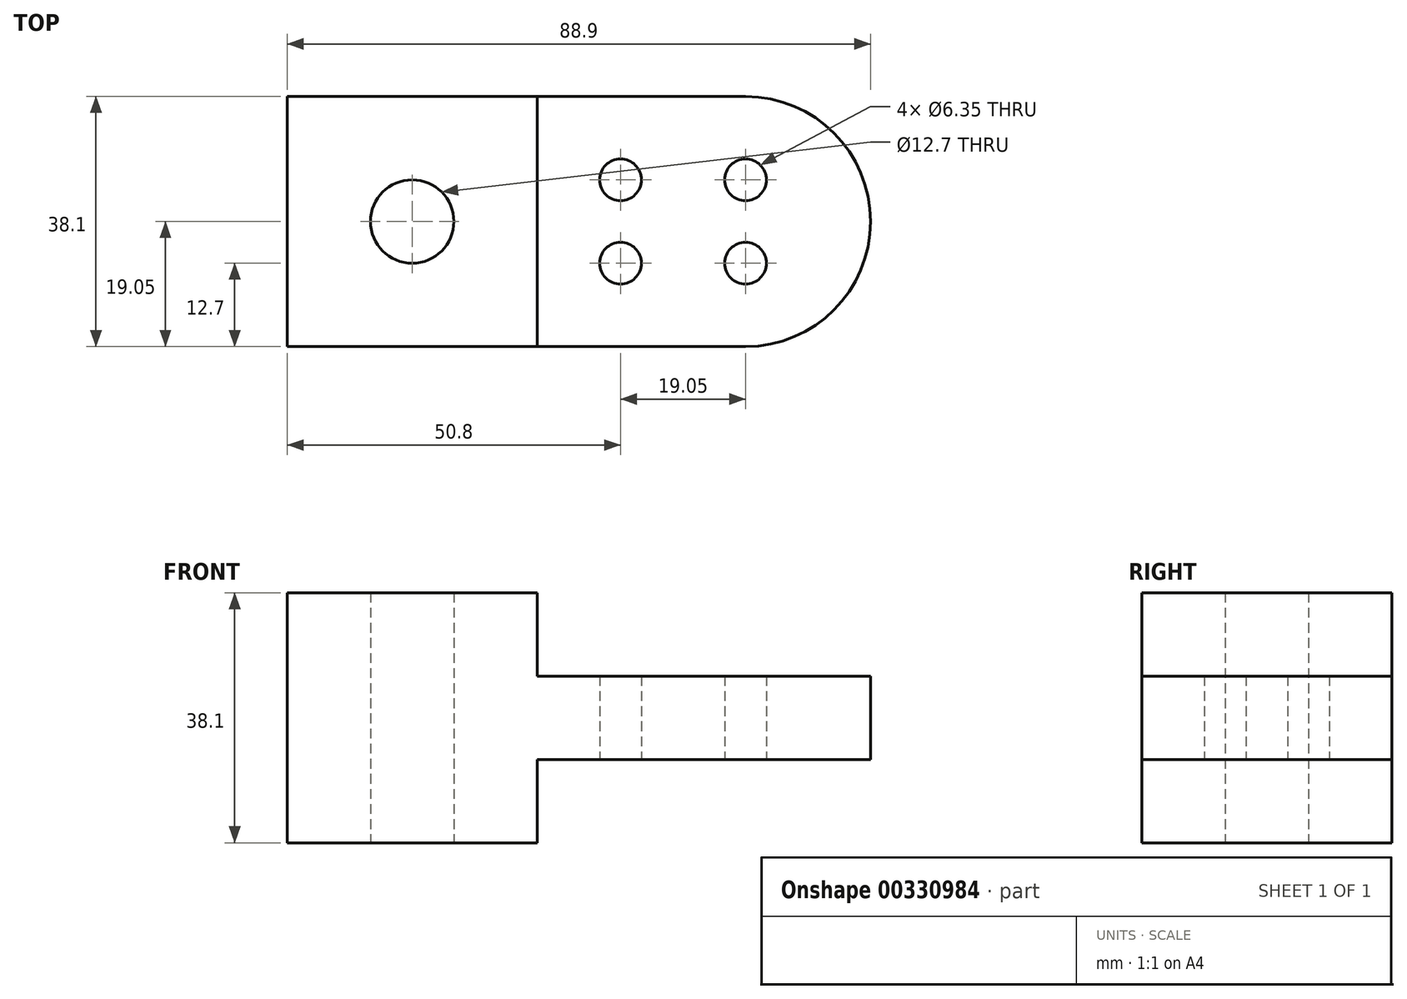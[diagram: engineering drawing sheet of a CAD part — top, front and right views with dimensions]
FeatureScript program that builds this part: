
annotation { "Feature Type Name" : "Feature", "Feature Type Description" : "" }
export const myFeature = defineFeature(function(context is Context, id is Id, definition is map)
    precondition{}
    {
        {
            var Q0;
            Q0=qCreatedBy(makeId("Top.planeOp"),FACE);
            var sketch = newSketch(context, id + "F0", { "sketchPlane" : qUnion([Q0])});
            skLineSegment(sketch, "E0.bottom", {"start": v(-19.05, 19.05) * mm, "end": v(19.05, 19.05) * mm});
            skLineSegment(sketch, "E0.top", {"start": v(-19.05, -19.05) * mm, "end": v(19.05, -19.05) * mm});
            skLineSegment(sketch, "E0.left", {"start": v(-19.05, 19.05) * mm, "end": v(-19.05, -19.05) * mm});
            skLineSegment(sketch, "E0.right", {"start": v(19.05, 19.05) * mm, "end": v(19.05, -19.05) * mm});
            skCircle(sketch, "E1", {"center": v(0, 0) * mm, "radius": 6.35 * mm});
            skSolve(sketch);
        }
        {
            var Q0;
            Q0 = qSketchRegion(id + "F0", true);
            extrude(context, id + "F1", {"entities" : qUnion([Q0]), "endBound" : BoundingType.SYMMETRIC, "depth" : 38.1 * mm});
        }
        {
            var Q0;
            Q0=qCreatedBy(makeId("Top.planeOp"),FACE);
            var sketch = newSketch(context, id + "F2", { "sketchPlane" : qUnion([Q0])});
            skLineSegment(sketch, "E2", {"start": v(19.05, 19.05) * mm, "end": v(50.8, 19.05) * mm});
            skArc(sketch, "E3", {"start": v(50.8, -19.05) * mm, "mid": v(69.85, 0) * mm, "end": v(50.8, 19.05) * mm});
            skLineSegment(sketch, "E4", {"start": v(50.8, -19.05) * mm, "end": v(19.05, -19.05) * mm});
            skLineSegment(sketch, "E5", {"start": v(19.05, 19.05) * mm, "end": v(19.05, -19.05) * mm});
            skCircle(sketch, "E6", {"center": v(31.75, -6.35) * mm, "radius": 3.18 * mm});
            skCircle(sketch, "E7", {"center": v(31.75, 6.35) * mm, "radius": 3.18 * mm});
            skCircle(sketch, "E8", {"center": v(50.8, 6.35) * mm, "radius": 3.18 * mm});
            skCircle(sketch, "E9", {"center": v(50.8, -6.35) * mm, "radius": 3.18 * mm});
            skSolve(sketch);
        }
        {
            var Q0;
            Q0 = qSketchRegion(id + "F2", true);
            extrude(context, id + "F3", {"entities" : qUnion([Q0]), "operationType" : NewBodyOperationType.ADD, "endBound" : BoundingType.SYMMETRIC, "depth" : 12.7 * mm});
        }
    });
